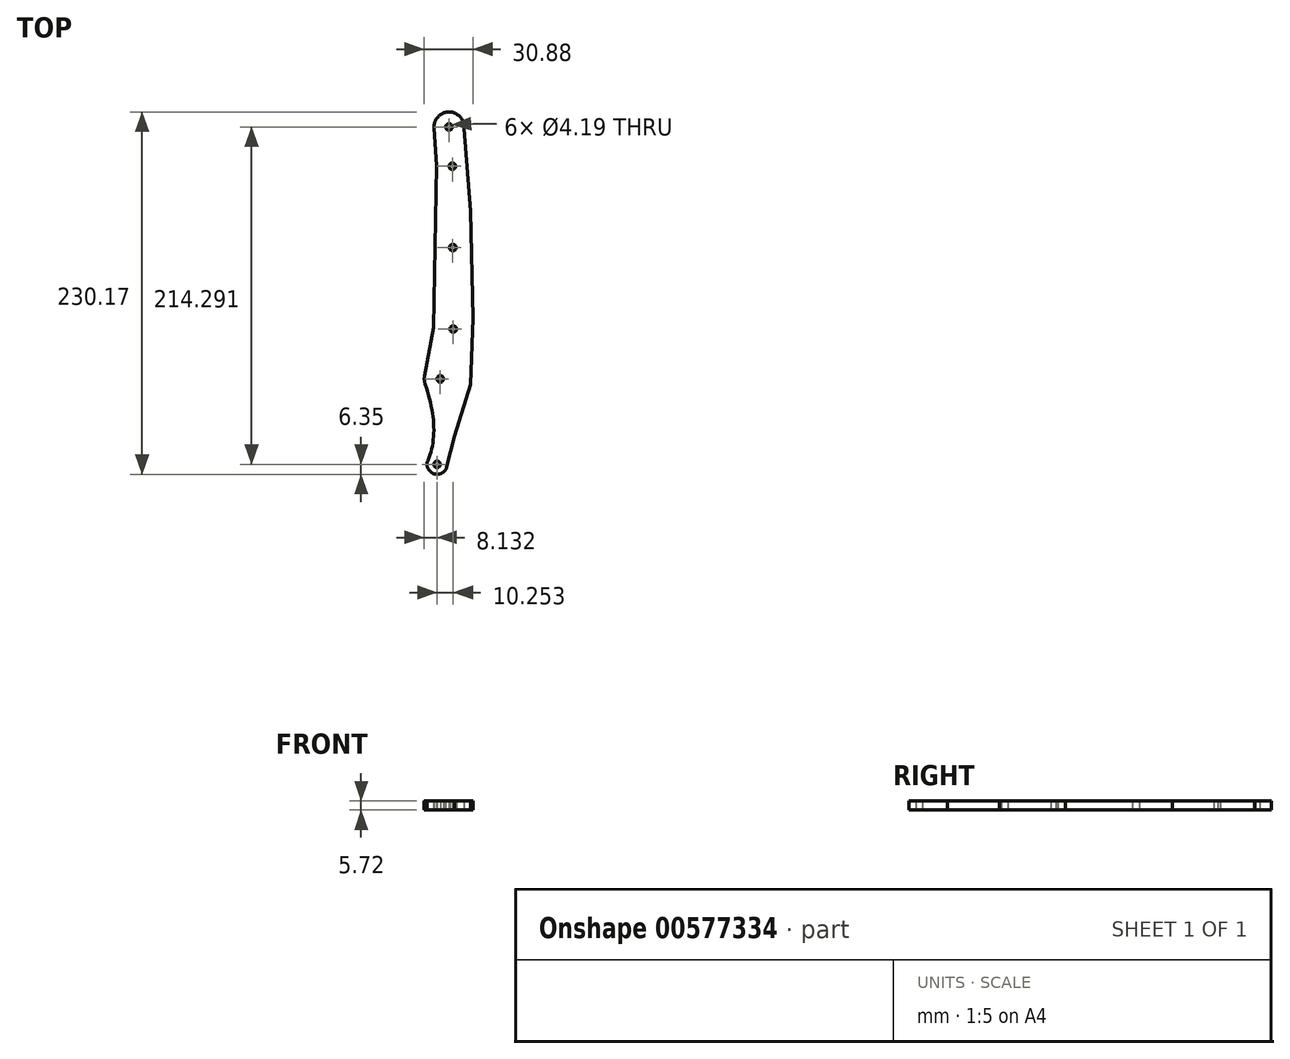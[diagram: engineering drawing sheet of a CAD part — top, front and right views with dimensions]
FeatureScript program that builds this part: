
annotation { "Feature Type Name" : "Feature", "Feature Type Description" : "" }
export const myFeature = defineFeature(function(context is Context, id is Id, definition is map)
    precondition{}
    {
        {
            var Q0;
            Q0=qCreatedBy(makeId("Top.planeOp"),FACE);
            var sketch = newSketch(context, id + "F0", { "sketchPlane" : qUnion([Q0])});
            skCircle(sketch, "E0", {"center": v(0.13, 105.56) * mm, "radius": 2.1 * mm});
            skCircle(sketch, "E1", {"center": v(2.25, 80.6) * mm, "radius": 2.1 * mm});
            skCircle(sketch, "E2", {"center": v(2.53, 28.93) * mm, "radius": 2.1 * mm});
            skCircle(sketch, "E3", {"center": v(2.8, -22.8) * mm, "radius": 2.1 * mm});
            skCircle(sketch, "E4", {"center": v(-5.43, -54.48) * mm, "radius": 2.1 * mm});
            skCircle(sketch, "E5", {"center": v(-7.46, -108.73) * mm, "radius": 2.1 * mm});
            skArc(sketch, "E6", {"start": v(-13.29, -106.2) * mm, "mid": v(-9.52, -114.74) * mm, "end": v(-1.31, -110.32) * mm});
            skArc(sketch, "E7", {"start": v(-15.42, -52.65) * mm, "mid": v(-15.56, -55.23) * mm, "end": v(-15.04, -57.76) * mm});
            skArc(sketch, "E8", {"start": v(9.6, 104.53) * mm, "mid": v(0.33, 115.08) * mm, "end": v(-9.37, 104.92) * mm});
            skLineSegment(sketch, "E9", {"start": v(13.69, -57.91) * mm, "end": v(3.76, -90.7) * mm});
            skLineSegment(sketch, "E10", {"start": v(3.76, -90.7) * mm, "end": v(-1.31, -110.32) * mm});
            skFitSpline(sketch, "E11", {"points": [v(-15.04, -57.76) * mm, v(-13.29, -106.2) * mm], "startDerivative": vector(19, -55.64) * mm, "endDerivative": vector(-17.47, -40.39) * mm});
            skLineSegment(sketch, "E12", {"start": v(-9.37, 104.92) * mm, "end": v(-7.77, 81.1) * mm});
            skLineSegment(sketch, "E13", {"start": v(-7.77, 81.1) * mm, "end": v(-9.78, -21.75) * mm});
            skLineSegment(sketch, "E14", {"start": v(-9.78, -21.75) * mm, "end": v(-15.42, -52.65) * mm});
            skLineSegment(sketch, "E15", {"start": v(9.6, 104.53) * mm, "end": v(13.8, 52.09) * mm});
            skLineSegment(sketch, "E16", {"start": v(13.8, 52.09) * mm, "end": v(15.29, -15.74) * mm});
            skLineSegment(sketch, "E17", {"start": v(15.29, -15.74) * mm, "end": v(13.69, -57.91) * mm});
            skSolve(sketch);
        }
        {
            var Q0;
            Q0 = qSketchRegion(id + "F0", true);
            extrude(context, id + "F1", {"entities" : qUnion([Q0]), "endBound" : BoundingType.SYMMETRIC, "depth" : 5.7 * mm, "offsetDistance" : 25.4 * mm});
        }
    });
